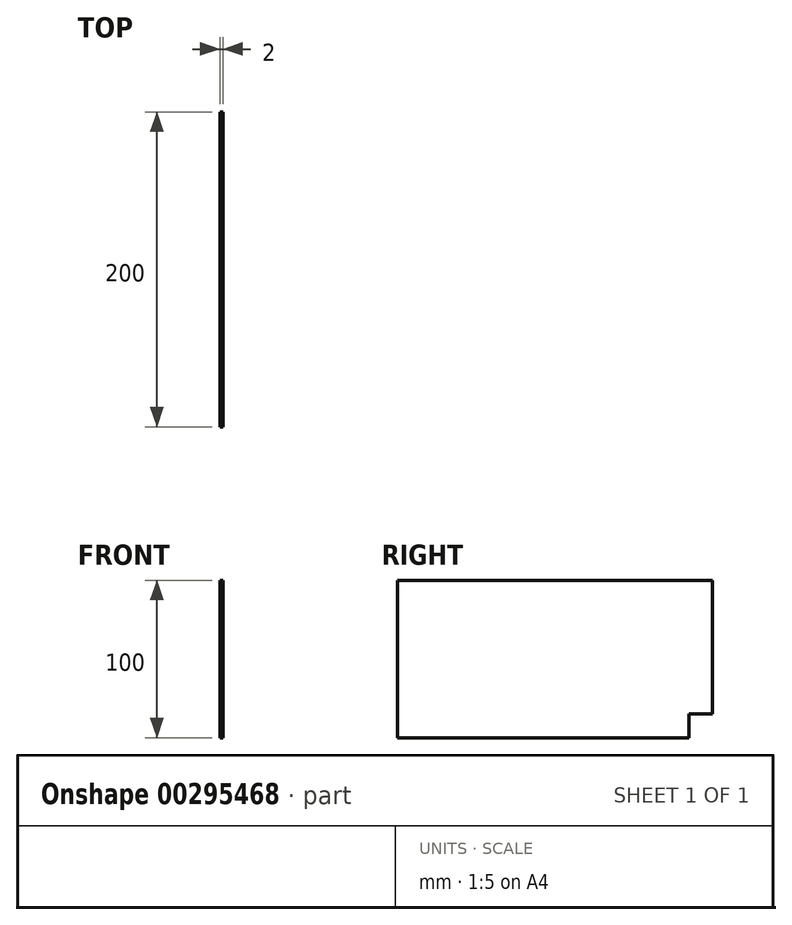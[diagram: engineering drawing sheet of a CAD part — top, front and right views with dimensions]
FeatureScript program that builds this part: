
annotation { "Feature Type Name" : "Feature", "Feature Type Description" : "" }
export const myFeature = defineFeature(function(context is Context, id is Id, definition is map)
    precondition{}
    {
        {
            var Q0;
            Q0=qCreatedBy(makeId("Right.planeOp"),FACE);
            var sketch = newSketch(context, id + "F0", { "sketchPlane" : qUnion([Q0])});
            skLineSegment(sketch, "E0", {"start": v(125.19, -47.17) * mm, "end": v(110.19, -47.17) * mm});
            skLineSegment(sketch, "E1", {"start": v(110.19, -47.17) * mm, "end": v(110.19, -62.17) * mm});
            skLineSegment(sketch, "E2", {"start": v(110.19, -62.17) * mm, "end": v(-74.81, -62.17) * mm});
            skLineSegment(sketch, "E3", {"start": v(-74.81, -62.17) * mm, "end": v(-74.81, 37.83) * mm});
            skLineSegment(sketch, "E4", {"start": v(-74.81, 37.83) * mm, "end": v(125.19, 37.83) * mm});
            skLineSegment(sketch, "E5", {"start": v(125.19, 37.83) * mm, "end": v(125.19, -47.17) * mm});
            skSolve(sketch);
        }
        {
            var Q0;
            Q0=makeQuery(id+"F0.imprint","IMPRINT",FACE,{"disambiguationData":[TD([[makeQuery(id+"F0.imprint","IMPRINT",EDGE,{"derivedFrom":sQuery(id+"F0.wireOp",EDGE,"E0")}),-1.0]])]});
            extrude(context, id + "F1", {"entities" : qUnion([Q0]), "depth" : 2 * mm});
        }
    });
